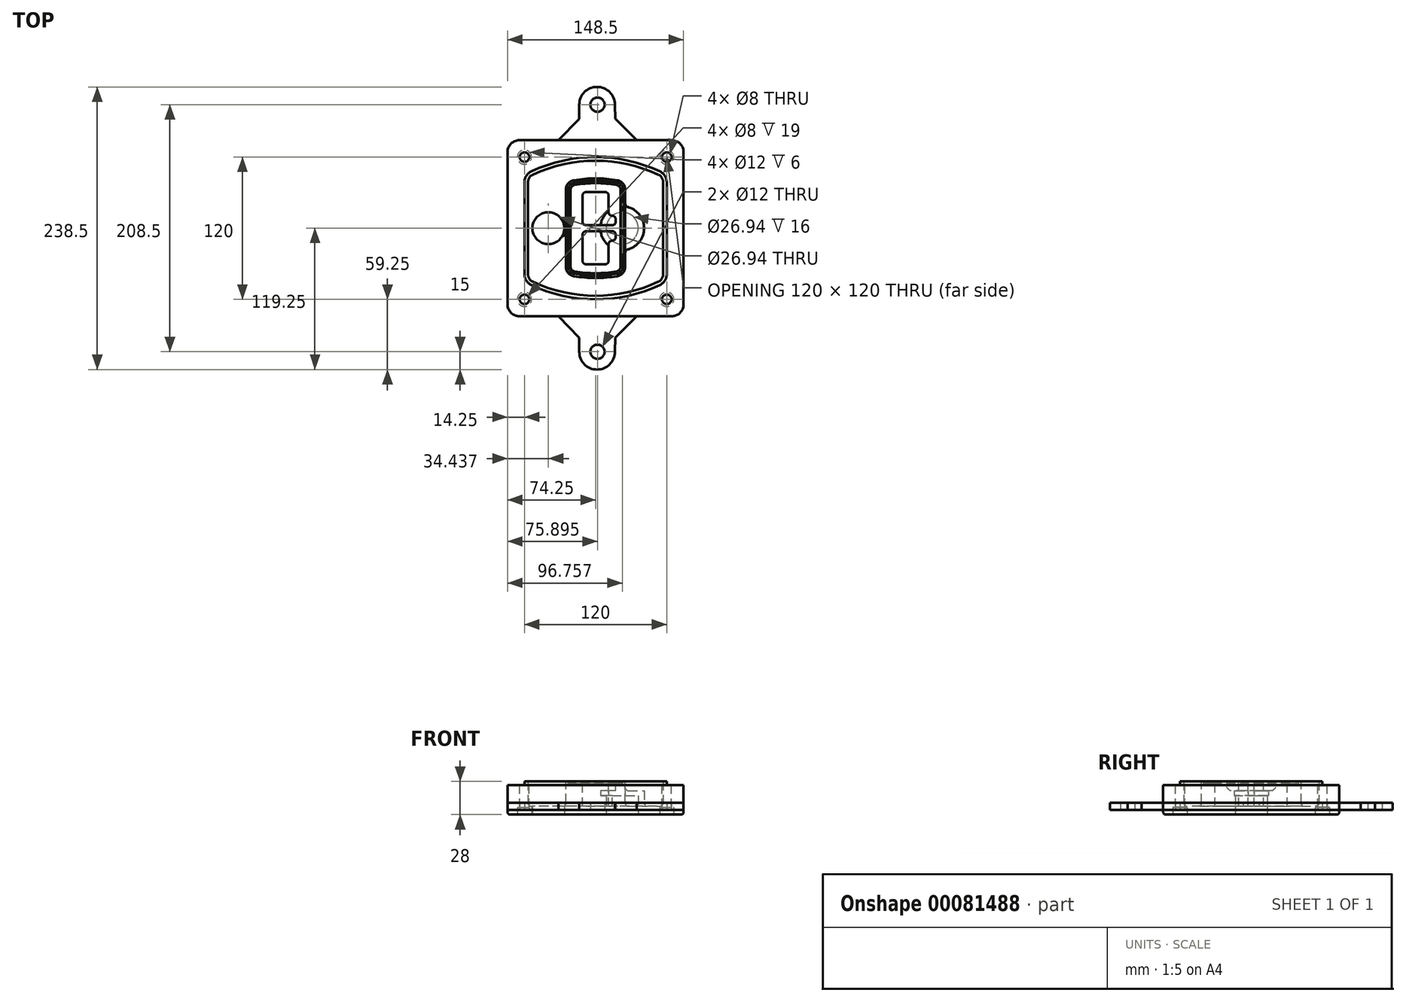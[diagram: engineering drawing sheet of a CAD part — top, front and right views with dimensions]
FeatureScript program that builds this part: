
annotation { "Feature Type Name" : "Feature", "Feature Type Description" : "" }
export const myFeature = defineFeature(function(context is Context, id is Id, definition is map)
    precondition{}
    {
        {
            var Q0;
            Q0=qCreatedBy(makeId("Top.planeOp"),FACE);
            var sketch = newSketch(context, id + "F0", { "sketchPlane" : qUnion([Q0])});
            skPoint(sketch, "E0.rect.middle", {"position": v(0, 0) * mm});
            skLineSegment(sketch, "E1.bottom", {"start": v(-64.25, -74.25) * mm, "end": v(64.25, -74.25) * mm});
            skLineSegment(sketch, "E1.top", {"start": v(-64.25, 74.25) * mm, "end": v(64.25, 74.25) * mm});
            skLineSegment(sketch, "E1.left", {"start": v(-74.25, -64.25) * mm, "end": v(-74.25, 64.25) * mm});
            skLineSegment(sketch, "E1.right", {"start": v(74.25, -64.25) * mm, "end": v(74.25, 64.25) * mm});
            skLineSegment(sketch, "E2", {"start": v(-74.25, 74.25) * mm, "end": v(74.25, -74.25) * mm, "construction": true});
            skLineSegment(sketch, "E3", {"start": v(74.25, 74.25) * mm, "end": v(-74.25, -74.25) * mm, "construction": true});
            skCircle(sketch, "E4", {"center": v(-60, 60) * mm, "radius": 4 * mm});
            skCircle(sketch, "E5", {"center": v(60, 60) * mm, "radius": 4 * mm});
            skCircle(sketch, "E6", {"center": v(60, -60) * mm, "radius": 4 * mm});
            skCircle(sketch, "E7", {"center": v(-60, -60) * mm, "radius": 4 * mm});
            skLineSegment(sketch, "E8", {"start": v(-60, 60) * mm, "end": v(60, 60) * mm, "construction": true});
            skLineSegment(sketch, "E9", {"start": v(60, 60) * mm, "end": v(60, -60) * mm, "construction": true});
            skLineSegment(sketch, "E10", {"start": v(60, -60) * mm, "end": v(-60, -60) * mm, "construction": true});
            skLineSegment(sketch, "E11", {"start": v(-60, -60) * mm, "end": v(-60, 60) * mm, "construction": true});
            skLineSegment(sketch, "E12", {"start": v(-60, 38.83) * mm, "end": v(-60, -38.83) * mm});
            skLineSegment(sketch, "E13", {"start": v(60, 38.83) * mm, "end": v(60, -38.83) * mm});
            skArc(sketch, "E14", {"start": v(54.26, 47.88) * mm, "mid": v(0, 60) * mm, "end": v(-54.26, 47.88) * mm});
            skArc(sketch, "E15", {"start": v(-54.26, -47.88) * mm, "mid": v(0, -60) * mm, "end": v(54.26, -47.88) * mm});
            skLineSegment(sketch, "E16", {"start": v(-60, 0) * mm, "end": v(60, 0) * mm, "construction": true});
            skPoint(sketch, "E17.visualSharp", {"position": v(-60, -45) * mm});
            skArc(sketch, "E17.filletArc", {"start": v(-60, -38.83) * mm, "mid": v(-58.44, -44.2) * mm, "end": v(-54.26, -47.88) * mm});
            skPoint(sketch, "E18.visualSharp", {"position": v(-60, 45) * mm});
            skArc(sketch, "E18.filletArc", {"start": v(-54.26, 47.88) * mm, "mid": v(-58.44, 44.2) * mm, "end": v(-60, 38.83) * mm});
            skPoint(sketch, "E19.visualSharp", {"position": v(60, 45) * mm});
            skArc(sketch, "E19.filletArc", {"start": v(60, 38.83) * mm, "mid": v(58.44, 44.2) * mm, "end": v(54.26, 47.88) * mm});
            skPoint(sketch, "E20.visualSharp", {"position": v(60, -45) * mm});
            skArc(sketch, "E20.filletArc", {"start": v(54.26, -47.88) * mm, "mid": v(58.44, -44.2) * mm, "end": v(60, -38.83) * mm});
            skPoint(sketch, "E21.visualSharp", {"position": v(-74.25, 74.25) * mm});
            skArc(sketch, "E21.filletArc", {"start": v(-64.25, 74.25) * mm, "mid": v(-71.32, 71.32) * mm, "end": v(-74.25, 64.25) * mm});
            skPoint(sketch, "E22.visualSharp", {"position": v(74.25, 74.25) * mm});
            skArc(sketch, "E22.filletArc", {"start": v(74.25, 64.25) * mm, "mid": v(71.32, 71.32) * mm, "end": v(64.25, 74.25) * mm});
            skPoint(sketch, "E23.visualSharp", {"position": v(74.25, -74.25) * mm});
            skArc(sketch, "E23.filletArc", {"start": v(64.25, -74.25) * mm, "mid": v(71.32, -71.32) * mm, "end": v(74.25, -64.25) * mm});
            skPoint(sketch, "E24.visualSharp", {"position": v(-74.25, -74.25) * mm});
            skArc(sketch, "E24.filletArc", {"start": v(-74.25, -64.25) * mm, "mid": v(-71.32, -71.32) * mm, "end": v(-64.25, -74.25) * mm});
            skArc(sketch, "E25.0", {"start": v(57, 38.83) * mm, "mid": v(55.9, 42.58) * mm, "end": v(52.98, 45.17) * mm});
            skLineSegment(sketch, "E25.1", {"start": v(57, 38.83) * mm, "end": v(57, -38.83) * mm});
            skArc(sketch, "E25.2", {"start": v(52.98, -45.17) * mm, "mid": v(55.9, -42.58) * mm, "end": v(57, -38.83) * mm});
            skArc(sketch, "E25.3", {"start": v(-52.98, -45.17) * mm, "mid": v(0, -57) * mm, "end": v(52.98, -45.17) * mm});
            skArc(sketch, "E25.4", {"start": v(-57, -38.83) * mm, "mid": v(-55.9, -42.58) * mm, "end": v(-52.98, -45.17) * mm});
            skArc(sketch, "E25.5", {"start": v(52.98, 45.17) * mm, "mid": v(0, 57) * mm, "end": v(-52.98, 45.17) * mm});
            skLineSegment(sketch, "E25.6", {"start": v(-57, 38.83) * mm, "end": v(-57, -38.83) * mm});
            skArc(sketch, "E25.7", {"start": v(-52.98, 45.17) * mm, "mid": v(-55.9, 42.58) * mm, "end": v(-57, 38.83) * mm});
            skArc(sketch, "E26.0", {"start": v(-55.96, 51.5) * mm, "mid": v(-61.82, 46.33) * mm, "end": v(-64, 38.83) * mm});
            skArc(sketch, "E26.1", {"start": v(55.96, 51.5) * mm, "mid": v(0, 64) * mm, "end": v(-55.96, 51.5) * mm});
            skArc(sketch, "E26.2", {"start": v(64, 38.83) * mm, "mid": v(61.82, 46.33) * mm, "end": v(55.96, 51.5) * mm});
            skLineSegment(sketch, "E26.3", {"start": v(64, 38.83) * mm, "end": v(64, -38.83) * mm});
            skArc(sketch, "E26.4", {"start": v(55.96, -51.5) * mm, "mid": v(61.82, -46.33) * mm, "end": v(64, -38.83) * mm});
            skLineSegment(sketch, "E26.5", {"start": v(-64, 38.83) * mm, "end": v(-64, -38.83) * mm});
            skArc(sketch, "E26.6", {"start": v(-55.96, -51.5) * mm, "mid": v(0, -64) * mm, "end": v(55.96, -51.5) * mm});
            skArc(sketch, "E26.7", {"start": v(-64, -38.83) * mm, "mid": v(-61.82, -46.33) * mm, "end": v(-55.96, -51.5) * mm});
            skSolve(sketch);
        }
        {
            var Q0;
            Q0=makeQuery(id+"F0.imprint","IMPRINT",FACE,{"disambiguationData":[TD([[makeQuery(id+"F0.imprint","IMPRINT",EDGE,{"derivedFrom":sQuery(id+"F0.wireOp",EDGE,"E1.bottom")}),1.0]])]});
            var Q1;
            Q1=makeQuery(id+"F0.imprint","IMPRINT",FACE,{"disambiguationData":[TD([[makeQuery(id+"F0.imprint","IMPRINT",EDGE,{"derivedFrom":sQuery(id+"F0.wireOp",EDGE,"E12")}),1.0]])]});
            var Q2;
            Q2=makeQuery(id+"F0.imprint","IMPRINT",FACE,{"disambiguationData":[TD([[makeQuery(id+"F0.imprint","IMPRINT",EDGE,{"derivedFrom":sQuery(id+"F0.wireOp",EDGE,"E25.0")}),1.0]])]});
            var Q3;
            Q3=makeQuery(id+"F0.imprint","IMPRINT",FACE,{"disambiguationData":[TD([[makeQuery(id+"F0.imprint","IMPRINT",EDGE,{"derivedFrom":sQuery(id+"F0.wireOp",EDGE,"E12")}),-1.0]])]});
            extrude(context, id + "F1", {"entities" : qUnion([Q0, Q1, Q2, Q3]), "oppositeDirection" : true, "depth" : 25 * mm});
        }
        {
            var Q0;
            Q0=makeQuery(id+"F0.imprint","IMPRINT",FACE,{"disambiguationData":[TD([[makeQuery(id+"F0.imprint","IMPRINT",EDGE,{"derivedFrom":sQuery(id+"F0.wireOp",EDGE,"E12")}),1.0]])]});
            extrude(context, id + "F2", {"entities" : qUnion([Q0]), "operationType" : NewBodyOperationType.ADD, "depth" : 3 * mm});
        }
        {
            var Q0;
            Q0=makeQuery(id+"F0.imprint","IMPRINT",FACE,{"disambiguationData":[TD([[makeQuery(id+"F0.imprint","IMPRINT",EDGE,{"derivedFrom":sQuery(id+"F0.wireOp",EDGE,"E25.0")}),1.0]])]});
            extrude(context, id + "F3", {"entities" : qUnion([Q0]), "operationType" : NewBodyOperationType.REMOVE, "oppositeDirection" : true, "depth" : 18 * mm});
        }
        {
            var Q0;
            Q0=makeQuery(id+"F2.opExtrude","CAP_FACE",FACE,{"disambiguationData":[OSD([sQuery(id+"F0.wireOp",EDGE,"E12"),sQuery(id+"F0.wireOp",EDGE,"E13"),sQuery(id+"F0.wireOp",EDGE,"E14"),sQuery(id+"F0.wireOp",EDGE,"E15"),sQuery(id+"F0.wireOp",EDGE,"E17.filletArc"),sQuery(id+"F0.wireOp",EDGE,"E18.filletArc"),sQuery(id+"F0.wireOp",EDGE,"E19.filletArc"),sQuery(id+"F0.wireOp",EDGE,"E20.filletArc"),sQuery(id+"F0.wireOp",EDGE,"E25.0"),sQuery(id+"F0.wireOp",EDGE,"E25.1"),sQuery(id+"F0.wireOp",EDGE,"E25.2"),sQuery(id+"F0.wireOp",EDGE,"E25.3"),sQuery(id+"F0.wireOp",EDGE,"E25.4"),sQuery(id+"F0.wireOp",EDGE,"E25.5"),sQuery(id+"F0.wireOp",EDGE,"E25.6"),sQuery(id+"F0.wireOp",EDGE,"E25.7")])],"isStart":false});
            var sketch = newSketch(context, id + "F4", { "sketchPlane" : qUnion([Q0])});
            skArc(sketch, "E27.0", {"start": v(-18.34, -40.45) * mm, "mid": v(0, -42) * mm, "end": v(18.34, -40.45) * mm});
            skArc(sketch, "E28.0", {"start": v(18.34, 40.45) * mm, "mid": v(0, 42) * mm, "end": v(-18.34, 40.45) * mm});
            skLineSegment(sketch, "E29", {"start": v(-25, 32.57) * mm, "end": v(-25, -32.57) * mm});
            skLineSegment(sketch, "E30", {"start": v(25, 32.57) * mm, "end": v(25, -32.57) * mm});
            skLineSegment(sketch, "E31", {"start": v(-25, 39.1) * mm, "end": v(25, 39.1) * mm, "construction": true});
            skLineSegment(sketch, "E32", {"start": v(-25, -39.1) * mm, "end": v(25, -39.1) * mm, "construction": true});
            skPoint(sketch, "E33.visualSharp", {"position": v(-25, 39.1) * mm});
            skArc(sketch, "E33.filletArc", {"start": v(-18.34, 40.45) * mm, "mid": v(-23.11, 37.73) * mm, "end": v(-25, 32.57) * mm});
            skPoint(sketch, "E34.visualSharp", {"position": v(25, 39.1) * mm});
            skArc(sketch, "E34.filletArc", {"start": v(25, 32.57) * mm, "mid": v(23.11, 37.73) * mm, "end": v(18.34, 40.45) * mm});
            skPoint(sketch, "E35.visualSharp", {"position": v(25, -39.1) * mm});
            skArc(sketch, "E35.filletArc", {"start": v(18.34, -40.45) * mm, "mid": v(23.11, -37.73) * mm, "end": v(25, -32.57) * mm});
            skPoint(sketch, "E36.visualSharp", {"position": v(-25, -39.1) * mm});
            skArc(sketch, "E36.filletArc", {"start": v(-25, -32.57) * mm, "mid": v(-23.11, -37.73) * mm, "end": v(-18.34, -40.45) * mm});
            skArc(sketch, "E37.0", {"start": v(52.98, 45.17) * mm, "mid": v(0, 57) * mm, "end": v(-52.98, 45.17) * mm});
            skArc(sketch, "E37.1", {"start": v(-52.98, 45.17) * mm, "mid": v(-55.9, 42.58) * mm, "end": v(-57, 38.83) * mm});
            skLineSegment(sketch, "E37.2", {"start": v(-57, 38.83) * mm, "end": v(-57, -38.83) * mm});
            skArc(sketch, "E37.3", {"start": v(-57, -38.83) * mm, "mid": v(-55.9, -42.58) * mm, "end": v(-52.98, -45.17) * mm});
            skArc(sketch, "E37.4", {"start": v(-52.98, -45.17) * mm, "mid": v(0, -57) * mm, "end": v(52.98, -45.17) * mm});
            skArc(sketch, "E37.5", {"start": v(52.98, -45.17) * mm, "mid": v(55.9, -42.58) * mm, "end": v(57, -38.83) * mm});
            skLineSegment(sketch, "E37.6", {"start": v(57, 38.83) * mm, "end": v(57, -38.83) * mm});
            skArc(sketch, "E37.7", {"start": v(57, 38.83) * mm, "mid": v(55.9, 42.58) * mm, "end": v(52.98, 45.17) * mm});
            skLineSegment(sketch, "E38.0", {"start": v(23, 32.57) * mm, "end": v(23, -32.57) * mm});
            skArc(sketch, "E38.1", {"start": v(18, -38.48) * mm, "mid": v(21.58, -36.44) * mm, "end": v(23, -32.57) * mm});
            skArc(sketch, "E38.2", {"start": v(-18, -38.48) * mm, "mid": v(0, -40) * mm, "end": v(18, -38.48) * mm});
            skArc(sketch, "E38.3", {"start": v(-23, -32.57) * mm, "mid": v(-21.58, -36.44) * mm, "end": v(-18, -38.48) * mm});
            skLineSegment(sketch, "E38.4", {"start": v(-23, 32.57) * mm, "end": v(-23, -32.57) * mm});
            skArc(sketch, "E38.5", {"start": v(23, 32.57) * mm, "mid": v(21.58, 36.44) * mm, "end": v(18, 38.48) * mm});
            skArc(sketch, "E38.6", {"start": v(-18, 38.48) * mm, "mid": v(-21.58, 36.44) * mm, "end": v(-23, 32.57) * mm});
            skArc(sketch, "E38.7", {"start": v(18, 38.48) * mm, "mid": v(0, 40) * mm, "end": v(-18, 38.48) * mm});
            skArc(sketch, "E39.0", {"start": v(21, 32.57) * mm, "mid": v(20.06, 35.15) * mm, "end": v(17.67, 36.5) * mm});
            skLineSegment(sketch, "E39.1", {"start": v(21, 32.57) * mm, "end": v(21, -32.57) * mm});
            skArc(sketch, "E39.2", {"start": v(17.67, -36.5) * mm, "mid": v(20.06, -35.15) * mm, "end": v(21, -32.57) * mm});
            skArc(sketch, "E39.3", {"start": v(-17.67, -36.5) * mm, "mid": v(0, -38) * mm, "end": v(17.67, -36.5) * mm});
            skArc(sketch, "E39.4", {"start": v(-21, -32.57) * mm, "mid": v(-20.06, -35.15) * mm, "end": v(-17.67, -36.5) * mm});
            skArc(sketch, "E39.5", {"start": v(17.67, 36.5) * mm, "mid": v(0, 38) * mm, "end": v(-17.67, 36.5) * mm});
            skLineSegment(sketch, "E39.6", {"start": v(-21, 32.57) * mm, "end": v(-21, -32.57) * mm});
            skArc(sketch, "E39.7", {"start": v(-17.67, 36.5) * mm, "mid": v(-20.06, 35.15) * mm, "end": v(-21, 32.57) * mm});
            skLineSegment(sketch, "E40", {"start": v(-25, 0) * mm, "end": v(25, 0) * mm, "construction": true});
            skLineSegment(sketch, "E41", {"start": v(-11, 5.5) * mm, "end": v(-11, 27.5) * mm});
            skLineSegment(sketch, "E42", {"start": v(-8, 30.5) * mm, "end": v(8, 30.5) * mm});
            skLineSegment(sketch, "E43", {"start": v(11, 27.5) * mm, "end": v(11, 13.5) * mm});
            skLineSegment(sketch, "E44", {"start": v(14, 10.5) * mm, "end": v(14, 10.5) * mm});
            skLineSegment(sketch, "E45", {"start": v(17, 7.5) * mm, "end": v(17, 5.5) * mm});
            skLineSegment(sketch, "E46", {"start": v(14, 2.5) * mm, "end": v(-8, 2.5) * mm});
            skPoint(sketch, "E47.visualSharp", {"position": v(-11, 30.5) * mm});
            skArc(sketch, "E47.filletArc", {"start": v(-8, 30.5) * mm, "mid": v(-10.12, 29.62) * mm, "end": v(-11, 27.5) * mm});
            skPoint(sketch, "E48.visualSharp", {"position": v(11, 30.5) * mm});
            skArc(sketch, "E48.filletArc", {"start": v(11, 27.5) * mm, "mid": v(10.12, 29.62) * mm, "end": v(8, 30.5) * mm});
            skPoint(sketch, "E49.visualSharp", {"position": v(11, 10.5) * mm});
            skArc(sketch, "E49.filletArc", {"start": v(11, 13.5) * mm, "mid": v(11.88, 11.38) * mm, "end": v(14, 10.5) * mm});
            skPoint(sketch, "E50.visualSharp", {"position": v(17, 10.5) * mm});
            skArc(sketch, "E50.filletArc", {"start": v(17, 7.5) * mm, "mid": v(16.12, 9.62) * mm, "end": v(14, 10.5) * mm});
            skPoint(sketch, "E51.visualSharp", {"position": v(17, 2.5) * mm});
            skArc(sketch, "E51.filletArc", {"start": v(14, 2.5) * mm, "mid": v(16.12, 3.38) * mm, "end": v(17, 5.5) * mm});
            skPoint(sketch, "E52.visualSharp", {"position": v(-11, 2.5) * mm});
            skArc(sketch, "E52.filletArc", {"start": v(-11, 5.5) * mm, "mid": v(-10.12, 3.38) * mm, "end": v(-8, 2.5) * mm});
            skLineSegment(sketch, "E53.0.MirrorCS", {"start": v(14, -2.5) * mm, "end": v(-8, -2.5) * mm});
            skArc(sketch, "E54.0.MirrorCS", {"start": v(-11, -5.5) * mm, "mid": v(-10.12, -3.38) * mm, "end": v(-8, -2.5) * mm});
            skLineSegment(sketch, "E55.0.MirrorCS", {"start": v(-11, -5.5) * mm, "end": v(-11, -27.5) * mm});
            skArc(sketch, "E56.0.MirrorCS", {"start": v(-8, -30.5) * mm, "mid": v(-10.12, -29.62) * mm, "end": v(-11, -27.5) * mm});
            skLineSegment(sketch, "E57.0.MirrorCS", {"start": v(-8, -30.5) * mm, "end": v(8, -30.5) * mm});
            skArc(sketch, "E58.0.MirrorCS", {"start": v(11, -27.5) * mm, "mid": v(10.12, -29.62) * mm, "end": v(8, -30.5) * mm});
            skLineSegment(sketch, "E59.0.MirrorCS", {"start": v(11, -27.5) * mm, "end": v(11, -13.5) * mm});
            skArc(sketch, "E60.0.MirrorCS", {"start": v(11, -13.5) * mm, "mid": v(11.88, -11.38) * mm, "end": v(14, -10.5) * mm});
            skArc(sketch, "E61.0.MirrorCS", {"start": v(17, -7.5) * mm, "mid": v(16.12, -9.62) * mm, "end": v(14, -10.5) * mm});
            skLineSegment(sketch, "E62.0.MirrorCS", {"start": v(17, -7.5) * mm, "end": v(17, -5.5) * mm});
            skArc(sketch, "E63.0.MirrorCS", {"start": v(14, -2.5) * mm, "mid": v(16.12, -3.38) * mm, "end": v(17, -5.5) * mm});
            skSolve(sketch);
        }
        {
            var Q0;
            Q0=makeQuery(id+"F4.imprint","IMPRINT",FACE,{"disambiguationData":[TD([[makeQuery(id+"F4.imprint","IMPRINT",EDGE,{"derivedFrom":sQuery(id+"F4.wireOp",EDGE,"E27.0")}),1.0]])]});
            var Q1;
            Q1=makeQuery(id+"F4.imprint","IMPRINT",FACE,{"disambiguationData":[TD([[makeQuery(id+"F4.imprint","IMPRINT",EDGE,{"derivedFrom":sQuery(id+"F4.wireOp",EDGE,"E38.0")}),-1.0]])]});
            var Q2;
            Q2=makeQuery(id+"F4.imprint","IMPRINT",FACE,{"disambiguationData":[TD([[makeQuery(id+"F4.imprint","IMPRINT",EDGE,{"derivedFrom":sQuery(id+"F4.wireOp",EDGE,"E39.0")}),1.0]])]});
            extrude(context, id + "F5", {"entities" : qUnion([Q0, Q1, Q2]), "operationType" : NewBodyOperationType.ADD, "endBound" : BoundingType.UP_TO_NEXT, "oppositeDirection" : true, "depth" : 25 * mm});
        }
        {
            var Q0;
            Q0=makeQuery(id+"F4.imprint","IMPRINT",FACE,{"disambiguationData":[TD([[makeQuery(id+"F4.imprint","IMPRINT",EDGE,{"derivedFrom":sQuery(id+"F4.wireOp",EDGE,"E38.0")}),-1.0]])]});
            extrude(context, id + "F6", {"entities" : qUnion([Q0]), "operationType" : NewBodyOperationType.REMOVE, "oppositeDirection" : true, "depth" : 2 * mm});
        }
        {
            var Q0;
            Q0=makeQuery(id+"F1.opExtrude","CAP_FACE",FACE,{"disambiguationData":[OSD([sQuery(id+"F0.wireOp",EDGE,"E1.bottom"),sQuery(id+"F0.wireOp",EDGE,"E1.top"),sQuery(id+"F0.wireOp",EDGE,"E1.left"),sQuery(id+"F0.wireOp",EDGE,"E1.right"),sQuery(id+"F0.wireOp",EDGE,"E4"),sQuery(id+"F0.wireOp",EDGE,"E5"),sQuery(id+"F0.wireOp",EDGE,"E6"),sQuery(id+"F0.wireOp",EDGE,"E7"),sQuery(id+"F0.wireOp",EDGE,"E21.filletArc"),sQuery(id+"F0.wireOp",EDGE,"E22.filletArc"),sQuery(id+"F0.wireOp",EDGE,"E23.filletArc"),sQuery(id+"F0.wireOp",EDGE,"E24.filletArc")])],"isStart":false});
            var sketch = newSketch(context, id + "F7", { "sketchPlane" : qUnion([Q0])});
            skCircle(sketch, "E64", {"center": v(22.5, 0) * mm, "radius": 13.47 * mm});
            skCircle(sketch, "E65", {"center": v(-39.81, 0) * mm, "radius": 13.47 * mm});
            skLineSegment(sketch, "E66", {"start": v(74.25, 0) * mm, "end": v(-74.25, 0) * mm});
            skCircle(sketch, "E67", {"center": v(22.5, 0) * mm, "radius": 18.47 * mm});
            skCircle(sketch, "E68", {"center": v(60, -60) * mm, "radius": 6 * mm});
            skCircle(sketch, "E69", {"center": v(-60, -60) * mm, "radius": 6 * mm});
            skCircle(sketch, "E70", {"center": v(-60, 60) * mm, "radius": 6 * mm});
            skCircle(sketch, "E71", {"center": v(60, 60) * mm, "radius": 6 * mm});
            skSolve(sketch);
        }
        {
            var Q0;
            {var subQ1=sQuery(id+"F7.wireOp",EDGE,"E66");var subQ4=sQuery(id+"F7.wireOp",EDGE,"E64");var subQ6=makeQuery(id+"F7.imprint","INTERSECT",VERTEX,{"disambiguationData":[OD(0.0)],"derivedFrom":[subQ4,subQ1]});Q0=makeQuery(id+"F7.imprint","IMPRINT",FACE,{"disambiguationData":[TD([[makeQuery(id+"F7.imprint","IMPRINT",EDGE,{"disambiguationData":[TD([[subQ6,-1.0]])],"derivedFrom":subQ4}),-1.0]])]});}
            var Q1;
            {var subQ0=sQuery(id+"F7.wireOp",EDGE,"E66");var subQ1=sQuery(id+"F7.wireOp",EDGE,"E64");var subQ3=makeQuery(id+"F7.imprint","INTERSECT",VERTEX,{"disambiguationData":[OD(0.0)],"derivedFrom":[subQ1,subQ0]});Q1=makeQuery(id+"F7.imprint","IMPRINT",FACE,{"disambiguationData":[TD([[makeQuery(id+"F7.imprint","IMPRINT",EDGE,{"disambiguationData":[TD([[subQ3,-1.0]])],"derivedFrom":subQ1}),1.0]])]});}
            var Q2;
            {var subQ0=sQuery(id+"F7.wireOp",EDGE,"E66");var subQ1=sQuery(id+"F7.wireOp",EDGE,"E64");var subQ3=makeQuery(id+"F7.imprint","INTERSECT",VERTEX,{"disambiguationData":[OD(0.0)],"derivedFrom":[subQ1,subQ0]});Q2=makeQuery(id+"F7.imprint","IMPRINT",FACE,{"disambiguationData":[TD([[makeQuery(id+"F7.imprint","IMPRINT",EDGE,{"disambiguationData":[TD([[subQ3,1.0]])],"derivedFrom":subQ1}),1.0]])]});}
            var Q3;
            {var subQ1=sQuery(id+"F7.wireOp",EDGE,"E66");var subQ4=sQuery(id+"F7.wireOp",EDGE,"E64");var subQ6=makeQuery(id+"F7.imprint","INTERSECT",VERTEX,{"disambiguationData":[OD(0.0)],"derivedFrom":[subQ4,subQ1]});Q3=makeQuery(id+"F7.imprint","IMPRINT",FACE,{"disambiguationData":[TD([[makeQuery(id+"F7.imprint","IMPRINT",EDGE,{"disambiguationData":[TD([[subQ6,1.0]])],"derivedFrom":subQ4}),-1.0]])]});}
            extrude(context, id + "F8", {"entities" : qUnion([Q0, Q1, Q2, Q3]), "operationType" : NewBodyOperationType.ADD, "oppositeDirection" : true, "depth" : 20 * mm});
        }
        {
            var Q0;
            {var subQ0=sQuery(id+"F7.wireOp",EDGE,"E66");var subQ1=sQuery(id+"F7.wireOp",EDGE,"E64");var subQ3=makeQuery(id+"F7.imprint","INTERSECT",VERTEX,{"disambiguationData":[OD(0.0)],"derivedFrom":[subQ1,subQ0]});Q0=makeQuery(id+"F7.imprint","IMPRINT",FACE,{"disambiguationData":[TD([[makeQuery(id+"F7.imprint","IMPRINT",EDGE,{"disambiguationData":[TD([[subQ3,-1.0]])],"derivedFrom":subQ1}),1.0]])]});}
            var Q1;
            {var subQ0=sQuery(id+"F7.wireOp",EDGE,"E66");var subQ1=sQuery(id+"F7.wireOp",EDGE,"E64");var subQ3=makeQuery(id+"F7.imprint","INTERSECT",VERTEX,{"disambiguationData":[OD(0.0)],"derivedFrom":[subQ1,subQ0]});Q1=makeQuery(id+"F7.imprint","IMPRINT",FACE,{"disambiguationData":[TD([[makeQuery(id+"F7.imprint","IMPRINT",EDGE,{"disambiguationData":[TD([[subQ3,1.0]])],"derivedFrom":subQ1}),1.0]])]});}
            extrude(context, id + "F9", {"entities" : qUnion([Q0, Q1]), "operationType" : NewBodyOperationType.REMOVE, "oppositeDirection" : true, "depth" : 16 * mm});
        }
        {
            var Q0;
            {var subQ0=sQuery(id+"F7.wireOp",EDGE,"E66");var subQ1=sQuery(id+"F7.wireOp",EDGE,"E65");var subQ3=makeQuery(id+"F7.imprint","INTERSECT",VERTEX,{"disambiguationData":[OD(0.0)],"derivedFrom":[subQ1,subQ0]});Q0=makeQuery(id+"F7.imprint","IMPRINT",FACE,{"disambiguationData":[TD([[makeQuery(id+"F7.imprint","IMPRINT",EDGE,{"disambiguationData":[TD([[subQ3,-1.0]])],"derivedFrom":subQ1}),1.0]])]});}
            var Q1;
            {var subQ0=sQuery(id+"F7.wireOp",EDGE,"E66");var subQ1=sQuery(id+"F7.wireOp",EDGE,"E65");var subQ3=makeQuery(id+"F7.imprint","INTERSECT",VERTEX,{"disambiguationData":[OD(0.0)],"derivedFrom":[subQ1,subQ0]});Q1=makeQuery(id+"F7.imprint","IMPRINT",FACE,{"disambiguationData":[TD([[makeQuery(id+"F7.imprint","IMPRINT",EDGE,{"disambiguationData":[TD([[subQ3,1.0]])],"derivedFrom":subQ1}),1.0]])]});}
            extrude(context, id + "F10", {"entities" : qUnion([Q0, Q1]), "operationType" : NewBodyOperationType.REMOVE, "oppositeDirection" : true, "depth" : 25 * mm});
        }
        {
            var Q0;
            Q0=makeQuery(id+"F7.imprint","IMPRINT",FACE,{"disambiguationData":[TD([[makeQuery(id+"F7.imprint","IMPRINT",EDGE,{"derivedFrom":sQuery(id+"F7.wireOp",EDGE,"E68")}),1.0]])]});
            var Q1;
            Q1=makeQuery(id+"F7.imprint","IMPRINT",FACE,{"disambiguationData":[TD([[makeQuery(id+"F7.imprint","IMPRINT",EDGE,{"derivedFrom":makeQuery(id+"F1.opExtrude","CAP_EDGE",EDGE,{"disambiguationData":[OSD([sQuery(id+"F0.wireOp",EDGE,"E5")])],"isStart":false})}),-1.0]])]});
            var Q2;
            Q2=makeQuery(id+"F7.imprint","IMPRINT",FACE,{"disambiguationData":[TD([[makeQuery(id+"F7.imprint","IMPRINT",EDGE,{"derivedFrom":sQuery(id+"F7.wireOp",EDGE,"E69")}),1.0]])]});
            var Q3;
            Q3=makeQuery(id+"F7.imprint","IMPRINT",FACE,{"disambiguationData":[TD([[makeQuery(id+"F7.imprint","IMPRINT",EDGE,{"derivedFrom":makeQuery(id+"F1.opExtrude","CAP_EDGE",EDGE,{"disambiguationData":[OSD([sQuery(id+"F0.wireOp",EDGE,"E4")])],"isStart":false})}),-1.0]])]});
            var Q4;
            Q4=makeQuery(id+"F7.imprint","IMPRINT",FACE,{"disambiguationData":[TD([[makeQuery(id+"F7.imprint","IMPRINT",EDGE,{"derivedFrom":sQuery(id+"F7.wireOp",EDGE,"E70")}),1.0]])]});
            var Q5;
            Q5=makeQuery(id+"F7.imprint","IMPRINT",FACE,{"disambiguationData":[TD([[makeQuery(id+"F7.imprint","IMPRINT",EDGE,{"derivedFrom":makeQuery(id+"F1.opExtrude","CAP_EDGE",EDGE,{"disambiguationData":[OSD([sQuery(id+"F0.wireOp",EDGE,"E7")])],"isStart":false})}),-1.0]])]});
            var Q6;
            Q6=makeQuery(id+"F7.imprint","IMPRINT",FACE,{"disambiguationData":[TD([[makeQuery(id+"F7.imprint","IMPRINT",EDGE,{"derivedFrom":sQuery(id+"F7.wireOp",EDGE,"E71")}),1.0]])]});
            var Q7;
            Q7=makeQuery(id+"F7.imprint","IMPRINT",FACE,{"disambiguationData":[TD([[makeQuery(id+"F7.imprint","IMPRINT",EDGE,{"derivedFrom":makeQuery(id+"F1.opExtrude","CAP_EDGE",EDGE,{"disambiguationData":[OSD([sQuery(id+"F0.wireOp",EDGE,"E6")])],"isStart":false})}),-1.0]])]});
            extrude(context, id + "F11", {"entities" : qUnion([Q0, Q1, Q2, Q3, Q4, Q5, Q6, Q7]), "operationType" : NewBodyOperationType.REMOVE, "oppositeDirection" : true, "depth" : 6 * mm});
        }
        {
            var Q0;
            Q0=makeQuery(id+"F9.boolean.opBoolean","COPY",FACE,{"derivedFrom":makeQuery(id+"F9.opExtrude","CAP_FACE",FACE,{"disambiguationData":[OSD([sQuery(id+"F7.wireOp",EDGE,"E64")])],"isStart":false})});
            var sketch = newSketch(context, id + "F12", { "sketchPlane" : qUnion([Q0])});
            skArc(sketch, "E72.0", {"start": v(11, 14.45) * mm, "mid": v(6.45, 9.13) * mm, "end": v(4.2, 2.5) * mm});
            skArc(sketch, "E72.1", {"start": v(4.2, -2.5) * mm, "mid": v(6.45, -9.13) * mm, "end": v(11, -14.45) * mm});
            skLineSegment(sketch, "E73", {"start": v(4.2, -2.5) * mm, "end": v(14, -2.5) * mm});
            skLineSegment(sketch, "E74.0", {"start": v(14, 2.5) * mm, "end": v(4.2, 2.5) * mm});
            skArc(sketch, "E74.1", {"start": v(14, 2.5) * mm, "mid": v(16.12, 3.38) * mm, "end": v(17, 5.5) * mm});
            skLineSegment(sketch, "E74.2", {"start": v(17, 7.5) * mm, "end": v(17, 5.5) * mm});
            skArc(sketch, "E74.3", {"start": v(17, 7.5) * mm, "mid": v(16.12, 9.62) * mm, "end": v(14, 10.5) * mm});
            skArc(sketch, "E74.4", {"start": v(11, 13.5) * mm, "mid": v(11.88, 11.38) * mm, "end": v(14, 10.5) * mm});
            skLineSegment(sketch, "E74.5", {"start": v(11, 14.45) * mm, "end": v(11, 13.5) * mm});
            skLineSegment(sketch, "E74.7", {"start": v(14, -2.5) * mm, "end": v(4.2, -2.5) * mm});
            skArc(sketch, "E74.8", {"start": v(14, -2.5) * mm, "mid": v(16.12, -3.38) * mm, "end": v(17, -5.5) * mm});
            skLineSegment(sketch, "E74.9", {"start": v(17, -7.5) * mm, "end": v(17, -5.5) * mm});
            skArc(sketch, "E74.10", {"start": v(17, -7.5) * mm, "mid": v(16.12, -9.62) * mm, "end": v(14, -10.5) * mm});
            skArc(sketch, "E74.11", {"start": v(11, -13.5) * mm, "mid": v(11.88, -11.38) * mm, "end": v(14, -10.5) * mm});
            skLineSegment(sketch, "E74.12", {"start": v(11, -14.45) * mm, "end": v(11, -13.5) * mm});
            skPoint(sketch, "E75.orphan", {"position": v(11, -27.5) * mm});
            skPoint(sketch, "E76.orphan", {"position": v(-8, -2.5) * mm});
            skPoint(sketch, "E77.orphan", {"position": v(-8, 2.5) * mm});
            skPoint(sketch, "E78.orphan", {"position": v(11, 27.5) * mm});
            skSolve(sketch);
        }
        {
            var Q0;
            {var subQ7=sQuery(id+"F12.wireOp",EDGE,"E72.0");var subQ14=sQuery(id+"F12.wireOp",EDGE,"E72.1");var subQ16=sQuery(id+"F12.wireOp",EDGE,"E74.1");var subQ18=sQuery(id+"F12.wireOp",EDGE,"E74.8");Q0=qUnion([makeQuery(id+"F12.imprint","IMPRINT",FACE,{"disambiguationData":[TD([[makeQuery(id+"F12.imprint","IMPRINT",EDGE,{"derivedFrom":subQ7}),1.0]])]}),makeQuery(id+"F12.imprint","IMPRINT",FACE,{"disambiguationData":[TD([[makeQuery(id+"F12.imprint","IMPRINT",EDGE,{"derivedFrom":subQ14}),1.0]])]}),makeQuery(id+"F12.imprint","IMPRINT",FACE,{"disambiguationData":[TD([[makeQuery(id+"F12.imprint","IMPRINT",EDGE,{"derivedFrom":subQ16}),1.0]])]}),makeQuery(id+"F12.imprint","IMPRINT",FACE,{"disambiguationData":[TD([[makeQuery(id+"F12.imprint","IMPRINT",EDGE,{"derivedFrom":subQ18}),-1.0]])]})]);}
            var Q1;
            Q1=makeQuery(id+"F5.boolean.opBoolean","SPLIT",FACE,{"disambiguationData":[TD([makeQuery(id+"F5.opExtrude","SWEPT_FACE",FACE,{"disambiguationData":[OSD([sQuery(id+"F4.wireOp",EDGE,"E41")])]})])],"derivedFrom":makeQuery(id+"F3.boolean.opBoolean","COPY",FACE,{"derivedFrom":makeQuery(id+"F3.opExtrude","CAP_FACE",FACE,{"disambiguationData":[OSD([sQuery(id+"F0.wireOp",EDGE,"E25.0"),sQuery(id+"F0.wireOp",EDGE,"E25.1"),sQuery(id+"F0.wireOp",EDGE,"E25.2"),sQuery(id+"F0.wireOp",EDGE,"E25.3"),sQuery(id+"F0.wireOp",EDGE,"E25.4"),sQuery(id+"F0.wireOp",EDGE,"E25.5"),sQuery(id+"F0.wireOp",EDGE,"E25.6"),sQuery(id+"F0.wireOp",EDGE,"E25.7")])],"isStart":false})})});
            extrude(context, id + "F13", {"entities" : qUnion([Q0]), "operationType" : NewBodyOperationType.REMOVE, "endBound" : BoundingType.UP_TO_SURFACE, "endBoundEntityFace" : qUnion([Q1]), "depth" : 25 * mm});
        }
        {
            var Q0;
            Q0=makeQuery(id+"F3.boolean.opBoolean","COPY",EDGE,{"derivedFrom":makeQuery(id+"F3.opExtrude","CAP_EDGE",EDGE,{"disambiguationData":[OSD([sQuery(id+"F0.wireOp",EDGE,"E25.6")])],"isStart":false})});
            var Q1;
            Q1=makeQuery(id+"F8.boolean.opBoolean","INTERSECT",EDGE,{"derivedFrom":[makeQuery(id+"F5.opExtrude","SWEPT_FACE",FACE,{"disambiguationData":[OSD([sQuery(id+"F4.wireOp",EDGE,"E30")])]}),makeQuery(id+"F8.opExtrude","CAP_FACE",FACE,{"disambiguationData":[OSD([sQuery(id+"F7.wireOp",EDGE,"E67")])],"isStart":false})]});
            var Q2;
            Q2=makeQuery(id+"F8.boolean.opBoolean","INTERSECT",EDGE,{"disambiguationData":[OD(1.0)],"derivedFrom":[makeQuery(id+"F5.opExtrude","SWEPT_FACE",FACE,{"disambiguationData":[OSD([sQuery(id+"F4.wireOp",EDGE,"E30")])]}),makeQuery(id+"F8.opExtrude","SWEPT_FACE",FACE,{"disambiguationData":[OSD([sQuery(id+"F7.wireOp",EDGE,"E67")])]})]});
            var Q3;
            {var subQ0=sQuery(id+"F4.wireOp",EDGE,"E30");Q3=makeQuery(id+"F8.boolean.opBoolean","SPLIT",EDGE,{"disambiguationData":[TD([makeQuery(id+"F5.opExtrude","SWEPT_FACE",FACE,{"disambiguationData":[OSD([sQuery(id+"F4.wireOp",EDGE,"E35.filletArc")])]})])],"derivedFrom":makeQuery(id+"F5.opExtrude","CAP_EDGE",EDGE,{"disambiguationData":[OSD([subQ0])],"isStart":false})});}
            var Q4;
            {var subQ0=sQuery(id+"F0.wireOp",EDGE,"E25.7");var subQ1=sQuery(id+"F0.wireOp",EDGE,"E25.1");var subQ2=sQuery(id+"F0.wireOp",EDGE,"E25.6");var subQ3=sQuery(id+"F0.wireOp",EDGE,"E25.5");var subQ4=sQuery(id+"F0.wireOp",EDGE,"E25.4");var subQ5=sQuery(id+"F0.wireOp",EDGE,"E25.0");var subQ6=sQuery(id+"F0.wireOp",EDGE,"E25.2");var subQ7=sQuery(id+"F0.wireOp",EDGE,"E25.3");Q4=makeQuery(id+"F8.boolean.opBoolean","INTERSECT",EDGE,{"derivedFrom":[makeQuery(id+"F5.boolean.opBoolean","SPLIT",FACE,{"disambiguationData":[TD([makeQuery(id+"F2.opExtrude","SWEPT_FACE",FACE,{"disambiguationData":[OSD([subQ5])]})])],"derivedFrom":makeQuery(id+"F3.boolean.opBoolean","COPY",FACE,{"derivedFrom":makeQuery(id+"F3.opExtrude","CAP_FACE",FACE,{"disambiguationData":[OSD([subQ5,subQ1,subQ6,subQ7,subQ4,subQ3,subQ2,subQ0])],"isStart":false})})}),makeQuery(id+"F8.opExtrude","SWEPT_FACE",FACE,{"disambiguationData":[OSD([sQuery(id+"F7.wireOp",EDGE,"E67")])]})]});}
            var Q5;
            Q5=makeQuery(id+"F8.boolean.opBoolean","INTERSECT",EDGE,{"disambiguationData":[OD(0.0)],"derivedFrom":[makeQuery(id+"F5.opExtrude","SWEPT_FACE",FACE,{"disambiguationData":[OSD([sQuery(id+"F4.wireOp",EDGE,"E30")])]}),makeQuery(id+"F8.opExtrude","SWEPT_FACE",FACE,{"disambiguationData":[OSD([sQuery(id+"F7.wireOp",EDGE,"E67")])]})]});
            fillet(context, id + "F14", {"entities" : qUnion([Q0, Q1, Q2, Q3, Q4, Q5]), "radius" : 3 * mm, "tangentPropagation" : true, "allowEdgeOverflow" : false});
        }
        {
            var Q0;
            Q0=makeQuery(id+"F1.opExtrude","CAP_EDGE",EDGE,{"disambiguationData":[OSD([sQuery(id+"F0.wireOp",EDGE,"E1.bottom")])],"isStart":false});
            fillet(context, id + "F15", {"entities" : qUnion([Q0]), "radius" : 2 * mm, "tangentPropagation" : true, "allowEdgeOverflow" : false});
        }
        {
            var Q0;
            {var subQ0=sQuery(id+"F0.wireOp",EDGE,"E25.7");var subQ1=sQuery(id+"F0.wireOp",EDGE,"E25.1");var subQ2=sQuery(id+"F0.wireOp",EDGE,"E25.6");var subQ3=sQuery(id+"F0.wireOp",EDGE,"E25.5");var subQ4=sQuery(id+"F0.wireOp",EDGE,"E25.4");var subQ5=sQuery(id+"F0.wireOp",EDGE,"E25.0");var subQ6=sQuery(id+"F0.wireOp",EDGE,"E25.2");var subQ7=sQuery(id+"F0.wireOp",EDGE,"E25.3");Q0=makeQuery(id+"F5.boolean.opBoolean","SPLIT",FACE,{"disambiguationData":[TD([makeQuery(id+"F2.opExtrude","SWEPT_FACE",FACE,{"disambiguationData":[OSD([subQ5])]})])],"derivedFrom":makeQuery(id+"F3.boolean.opBoolean","COPY",FACE,{"derivedFrom":makeQuery(id+"F3.opExtrude","CAP_FACE",FACE,{"disambiguationData":[OSD([subQ5,subQ1,subQ6,subQ7,subQ4,subQ3,subQ2,subQ0])],"isStart":false})})});}
            var sketch = newSketch(context, id + "F16", { "sketchPlane" : qUnion([Q0])});
            skArc(sketch, "E79.0.0", {"start": v(-74.25, -64.25) * mm, "mid": v(-71.32, -71.32) * mm, "end": v(-64.25, -74.25) * mm});
            skLineSegment(sketch, "E79.0.1", {"start": v(-64.25, -74.25) * mm, "end": v(64.25, -74.25) * mm});
            skArc(sketch, "E79.0.2", {"start": v(64.25, -74.25) * mm, "mid": v(71.32, -71.32) * mm, "end": v(74.25, -64.25) * mm});
            skLineSegment(sketch, "E79.0.3", {"start": v(74.25, -64.25) * mm, "end": v(74.25, 64.25) * mm});
            skArc(sketch, "E79.0.4", {"start": v(74.25, 64.25) * mm, "mid": v(71.32, 71.32) * mm, "end": v(64.25, 74.25) * mm});
            skLineSegment(sketch, "E79.0.5", {"start": v(64.25, 74.25) * mm, "end": v(-64.25, 74.25) * mm});
            skArc(sketch, "E79.0.6", {"start": v(-64.25, 74.25) * mm, "mid": v(-71.32, 71.32) * mm, "end": v(-74.25, 64.25) * mm});
            skLineSegment(sketch, "E79.0.7", {"start": v(-74.25, 64.25) * mm, "end": v(-74.25, -64.25) * mm});
            skArc(sketch, "E79.1", {"start": v(54.26, 47.88) * mm, "mid": v(0, 60) * mm, "end": v(-54.26, 47.88) * mm});
            skArc(sketch, "E79.2", {"start": v(-54.26, 47.88) * mm, "mid": v(-58.44, 44.2) * mm, "end": v(-60, 38.83) * mm});
            skLineSegment(sketch, "E79.3", {"start": v(-60, 38.83) * mm, "end": v(-60, -38.83) * mm});
            skArc(sketch, "E79.4", {"start": v(-60, -38.83) * mm, "mid": v(-58.44, -44.2) * mm, "end": v(-54.26, -47.88) * mm});
            skArc(sketch, "E79.5", {"start": v(-54.26, -47.88) * mm, "mid": v(0, -60) * mm, "end": v(54.26, -47.88) * mm});
            skArc(sketch, "E79.6", {"start": v(54.26, -47.88) * mm, "mid": v(58.44, -44.2) * mm, "end": v(60, -38.83) * mm});
            skLineSegment(sketch, "E79.7", {"start": v(60, 38.83) * mm, "end": v(60, -38.83) * mm});
            skArc(sketch, "E79.8", {"start": v(60, 38.83) * mm, "mid": v(58.44, 44.2) * mm, "end": v(54.26, 47.88) * mm});
            skCircle(sketch, "E79.9", {"center": v(60, 60) * mm, "radius": 4 * mm});
            skCircle(sketch, "E79.10", {"center": v(-60, 60) * mm, "radius": 4 * mm});
            skCircle(sketch, "E79.11", {"center": v(-60, -60) * mm, "radius": 4 * mm});
            skCircle(sketch, "E79.12", {"center": v(60, -60) * mm, "radius": 4 * mm});
            skArc(sketch, "E79.14", {"start": v(-64.25, 74.25) * mm, "mid": v(-71.32, 71.32) * mm, "end": v(-74.25, 64.25) * mm});
            skLineSegment(sketch, "E79.15", {"start": v(-74.25, -64.25) * mm, "end": v(-74.25, 64.25) * mm});
            skArc(sketch, "E79.16", {"start": v(-74.25, -64.25) * mm, "mid": v(-71.32, -71.32) * mm, "end": v(-64.25, -74.25) * mm});
            skLineSegment(sketch, "E79.17", {"start": v(-64.25, -74.25) * mm, "end": v(64.25, -74.25) * mm});
            skArc(sketch, "E79.18", {"start": v(64.25, -74.25) * mm, "mid": v(71.32, -71.32) * mm, "end": v(74.25, -64.25) * mm});
            skLineSegment(sketch, "E79.19", {"start": v(74.25, -64.25) * mm, "end": v(74.25, 64.25) * mm});
            skArc(sketch, "E79.20", {"start": v(74.25, 64.25) * mm, "mid": v(71.32, 71.32) * mm, "end": v(64.25, 74.25) * mm});
            skLineSegment(sketch, "E80", {"start": v(16.24, 104.25) * mm, "end": v(16.48, 92.42) * mm});
            skLineSegment(sketch, "E81", {"start": v(-13.76, 104.25) * mm, "end": v(-13.76, 92.25) * mm});
            skLineSegment(sketch, "E82", {"start": v(-64.25, 74.25) * mm, "end": v(64.25, 74.25) * mm});
            skLineSegment(sketch, "E83", {"start": v(-31.36, 74.25) * mm, "end": v(34.64, 74.25) * mm});
            skLineSegment(sketch, "E84", {"start": v(1.64, 74.25) * mm, "end": v(1.64, 104.25) * mm, "construction": true});
            skLineSegment(sketch, "E85", {"start": v(-13.76, 92.25) * mm, "end": v(-31.36, 74.25) * mm});
            skLineSegment(sketch, "E86", {"start": v(16.48, 92.42) * mm, "end": v(34.64, 74.25) * mm});
            skArc(sketch, "E87", {"start": v(16.24, 104.25) * mm, "mid": v(1.24, 119.25) * mm, "end": v(-13.76, 104.25) * mm});
            skCircle(sketch, "E88", {"center": v(1.64, 104.25) * mm, "radius": 6 * mm});
            skLineSegment(sketch, "E89", {"start": v(-74.25, 0) * mm, "end": v(74.25, 0) * mm, "construction": true});
            skArc(sketch, "E90.MirrorCS", {"start": v(16.24, -104.25) * mm, "mid": v(1.24, -119.25) * mm, "end": v(-13.76, -104.25) * mm});
            skCircle(sketch, "E91.MirrorC", {"center": v(1.64, -104.25) * mm, "radius": 6 * mm});
            skLineSegment(sketch, "E92.MirrorCS", {"start": v(16.24, -104.25) * mm, "end": v(16.48, -92.42) * mm});
            skLineSegment(sketch, "E93.MirrorCS", {"start": v(-13.76, -104.25) * mm, "end": v(-13.76, -92.25) * mm});
            skLineSegment(sketch, "E94.MirrorCS", {"start": v(-13.76, -92.25) * mm, "end": v(-31.36, -74.25) * mm});
            skLineSegment(sketch, "E95.MirrorCS", {"start": v(16.48, -92.42) * mm, "end": v(34.64, -74.25) * mm});
            skLineSegment(sketch, "E96.MirrorCS", {"start": v(1.64, -74.25) * mm, "end": v(1.64, -104.25) * mm, "construction": true});
            skSolve(sketch);
        }
        {
            var Q0;
            Q0 = qSketchRegion(id + "F16", true);
            extrude(context, id + "F17", {"entities" : qUnion([Q0]), "endBound" : BoundingType.SYMMETRIC, "depth" : 6 * mm});
        }
    });
